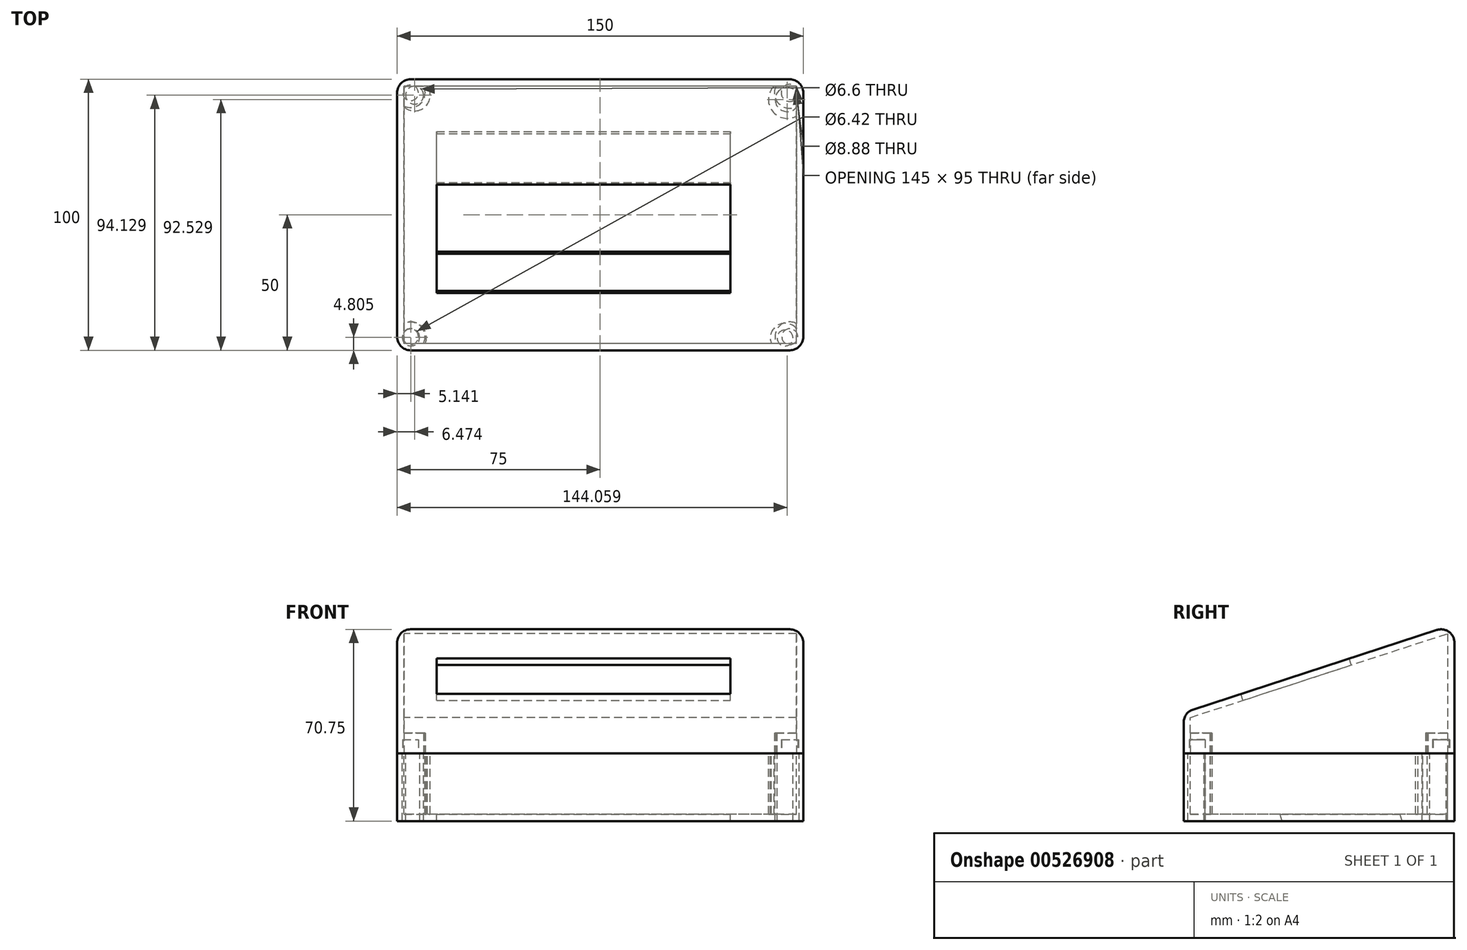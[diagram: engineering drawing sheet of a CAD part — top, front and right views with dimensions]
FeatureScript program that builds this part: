
annotation { "Feature Type Name" : "Feature", "Feature Type Description" : "" }
export const myFeature = defineFeature(function(context is Context, id is Id, definition is map)
    precondition{}
    {
        {
            var Q0;
            Q0=qCreatedBy(makeId("Top.planeOp"),FACE);
            var sketch = newSketch(context, id + "F0", { "sketchPlane" : qUnion([Q0])});
            skLineSegment(sketch, "E0.bottom", {"start": v(75, 50) * mm, "end": v(-75, 50) * mm});
            skLineSegment(sketch, "E0.top", {"start": v(75, -50) * mm, "end": v(-75, -50) * mm});
            skLineSegment(sketch, "E0.left", {"start": v(75, 50) * mm, "end": v(75, -50) * mm});
            skLineSegment(sketch, "E0.right", {"start": v(-75, 50) * mm, "end": v(-75, -50) * mm});
            skPoint(sketch, "E0.middle", {"position": v(0, 0) * mm});
            skSolve(sketch);
        }
        {
            var Q0;
            Q0=makeQuery(id+"F0.imprint","IMPRINT",FACE,{"disambiguationData":[TD([[makeQuery(id+"F0.imprint","IMPRINT",EDGE,{"derivedFrom":sQuery(id+"F0.wireOp",EDGE,"E0.bottom")}),1.0]])]});
            extrude(context, id + "F1", {"entities" : qUnion([Q0]), "depth" : 25 * mm, "offsetDistance" : 25 * mm});
        }
        {
            var Q0;
            Q0=makeQuery(id+"F1.opExtrude","CAP_FACE",FACE,{"disambiguationData":[OSD([sQuery(id+"F0.wireOp",EDGE,"E0.bottom"),sQuery(id+"F0.wireOp",EDGE,"E0.top"),sQuery(id+"F0.wireOp",EDGE,"E0.left"),sQuery(id+"F0.wireOp",EDGE,"E0.right")])],"isStart":false});
            var sketch = newSketch(context, id + "F2", { "sketchPlane" : qUnion([Q0])});
            skCircle(sketch, "E1", {"center": v(-68.53, 44.13) * mm, "radius": 3.3 * mm});
            skCircle(sketch, "E2", {"center": v(-69.86, -45.2) * mm, "radius": 3.21 * mm});
            skCircle(sketch, "E3", {"center": v(68.26, -45.46) * mm, "radius": 2.93 * mm});
            skCircle(sketch, "E4", {"center": v(69.06, 42.53) * mm, "radius": 4.44 * mm});
            skSolve(sketch);
        }
        {
            var Q0;
            Q0 = qSketchRegion(id + "F2", true);
            extrude(context, id + "F3", {"entities" : qUnion([Q0]), "operationType" : NewBodyOperationType.REMOVE, "endBound" : BoundingType.THROUGH_ALL, "oppositeDirection" : true, "depth" : 25 * mm, "offsetDistance" : 25 * mm});
        }
        {
            var Q0;
            Q0=makeQuery(id+"F1.opExtrude","CAP_FACE",FACE,{"disambiguationData":[OSD([sQuery(id+"F0.wireOp",EDGE,"E0.bottom"),sQuery(id+"F0.wireOp",EDGE,"E0.top"),sQuery(id+"F0.wireOp",EDGE,"E0.left"),sQuery(id+"F0.wireOp",EDGE,"E0.right")])],"isStart":false});
            shell(context, id + "F4", {"entities" : qUnion([Q0]), "thickness" : 2.5 * mm});
        }
        {
            var Q0;
            Q0=makeQuery(id+"F1.opExtrude","SWEPT_FACE",FACE,{"disambiguationData":[OSD([sQuery(id+"F0.wireOp",EDGE,"E0.right")])]});
            var sketch = newSketch(context, id + "F5", { "sketchPlane" : qUnion([Q0])});
            skLineSegment(sketch, "E5", {"start": v(-50, 25) * mm, "end": v(50, 25) * mm});
            skLineSegment(sketch, "E6", {"start": v(50, 25) * mm, "end": v(50, 40.03) * mm});
            skLineSegment(sketch, "E7", {"start": v(50, 40.03) * mm, "end": v(-50, 72.64) * mm});
            skLineSegment(sketch, "E8", {"start": v(-50, 72.64) * mm, "end": v(-50, 25) * mm});
            skSolve(sketch);
        }
        {
            var Q0;
            Q0 = qSketchRegion(id + "F5", true);
            var Q1;
            Q1=makeQuery(id+"F1.opExtrude","SWEPT_FACE",FACE,{"disambiguationData":[OSD([sQuery(id+"F0.wireOp",EDGE,"E0.left")])]});
            extrude(context, id + "F6", {"entities" : qUnion([Q0]), "endBound" : BoundingType.UP_TO_SURFACE, "oppositeDirection" : true, "depth" : 25 * mm, "endBoundEntityFace" : qUnion([Q1]), "offsetDistance" : 25 * mm});
        }
        {
            var Q0;
            Q0=makeQuery(id+"F6.opExtrude","SWEPT_FACE",FACE,{"disambiguationData":[OSD([sQuery(id+"F5.wireOp",EDGE,"E5")])]});
            var sketch = newSketch(context, id + "F7", { "sketchPlane" : qUnion([Q0])});
            skCircle(sketch, "E9", {"center": v(-70, 45) * mm, "radius": 2.87 * mm});
            skCircle(sketch, "E10", {"center": v(-70, -45) * mm, "radius": 2.9 * mm});
            skCircle(sketch, "E11", {"center": v(70, -45) * mm, "radius": 3.18 * mm});
            skCircle(sketch, "E12", {"center": v(70, 45) * mm, "radius": 2.94 * mm});
            skSolve(sketch);
        }
        {
            var Q0;
            Q0 = qSketchRegion(id + "F7", true);
            extrude(context, id + "F8", {"entities" : qUnion([Q0]), "operationType" : NewBodyOperationType.REMOVE, "oppositeDirection" : true, "depth" : 5 * mm, "offsetDistance" : 25 * mm});
        }
        {
            var Q0;
            Q0=makeQuery(id+"F6.opExtrude","SWEPT_FACE",FACE,{"disambiguationData":[OSD([sQuery(id+"F5.wireOp",EDGE,"E5")])]});
            shell(context, id + "F9", {"entities" : qUnion([Q0]), "thickness" : 2.5 * mm});
        }
        {
            var Q0;
            Q0=makeQuery(id+"F6.opExtrude","SWEPT_FACE",FACE,{"disambiguationData":[OSD([sQuery(id+"F5.wireOp",EDGE,"E7")])]});
            var sketch = newSketch(context, id + "F10", { "sketchPlane" : qUnion([Q0])});
            skLineSegment(sketch, "E13.bottom", {"start": v(-60.4, -12.93) * mm, "end": v(48.13, -12.93) * mm});
            skLineSegment(sketch, "E13.top", {"start": v(-60.4, 29.2) * mm, "end": v(48.13, 29.2) * mm});
            skLineSegment(sketch, "E13.left", {"start": v(-60.4, -12.93) * mm, "end": v(-60.4, 29.2) * mm});
            skLineSegment(sketch, "E13.right", {"start": v(48.13, -12.93) * mm, "end": v(48.13, 29.2) * mm});
            skSolve(sketch);
        }
        {
            var Q0;
            Q0 = qSketchRegion(id + "F10", true);
            extrude(context, id + "F11", {"entities" : qUnion([Q0]), "operationType" : NewBodyOperationType.REMOVE, "endBound" : BoundingType.THROUGH_ALL, "oppositeDirection" : true, "depth" : 25 * mm, "offsetDistance" : 25 * mm});
        }
        {
            var Q0;
            Q0=makeQuery(id+"F6.opExtrude","SWEPT_EDGE",EDGE,{"disambiguationData":[OSD([sQuery(id+"F5.wireOp",EDGE,"E7"),sQuery(id+"F5.wireOp",EDGE,"E8")])]});
            var Q1;
            Q1=makeQuery(id+"F6.opExtrude","CAP_EDGE",EDGE,{"disambiguationData":[OSD([sQuery(id+"F5.wireOp",EDGE,"E7")])],"isStart":true});
            var Q2;
            Q2=makeQuery(id+"F6.opExtrude","CAP_EDGE",EDGE,{"disambiguationData":[OSD([sQuery(id+"F5.wireOp",EDGE,"E7")])],"isStart":false});
            var Q3;
            Q3=makeQuery(id+"F6.opExtrude","SWEPT_EDGE",EDGE,{"disambiguationData":[OSD([sQuery(id+"F5.wireOp",EDGE,"E6"),sQuery(id+"F5.wireOp",EDGE,"E7")])]});
            var Q4;
            Q4=makeQuery(id+"F6.opExtrude","CAP_EDGE",EDGE,{"disambiguationData":[OSD([sQuery(id+"F5.wireOp",EDGE,"E6")])],"isStart":true});
            var Q5;
            Q5=makeQuery(id+"F6.opExtrude","CAP_EDGE",EDGE,{"disambiguationData":[OSD([sQuery(id+"F5.wireOp",EDGE,"E6")])],"isStart":false});
            var Q6;
            Q6=makeQuery(id+"F6.opExtrude","CAP_EDGE",EDGE,{"disambiguationData":[OSD([sQuery(id+"F5.wireOp",EDGE,"E8")])],"isStart":false});
            var Q7;
            Q7=makeQuery(id+"F6.opExtrude","CAP_EDGE",EDGE,{"disambiguationData":[OSD([sQuery(id+"F5.wireOp",EDGE,"E8")])],"isStart":true});
            fillet(context, id + "F12", {"entities" : qUnion([Q0, Q1, Q2, Q3, Q4, Q5, Q6, Q7]), "radius" : 5 * mm, "tangentPropagation" : true, "allowEdgeOverflow" : false});
        }
        {
            var Q0;
            Q0=makeQuery(id+"F1.opExtrude","SWEPT_EDGE",EDGE,{"disambiguationData":[OSD([sQuery(id+"F0.wireOp",EDGE,"E0.top"),sQuery(id+"F0.wireOp",EDGE,"E0.right")])]});
            var Q1;
            Q1=makeQuery(id+"F1.opExtrude","SWEPT_EDGE",EDGE,{"disambiguationData":[OSD([sQuery(id+"F0.wireOp",EDGE,"E0.top"),sQuery(id+"F0.wireOp",EDGE,"E0.left")])]});
            var Q2;
            Q2=makeQuery(id+"F1.opExtrude","SWEPT_EDGE",EDGE,{"disambiguationData":[OSD([sQuery(id+"F0.wireOp",EDGE,"E0.bottom"),sQuery(id+"F0.wireOp",EDGE,"E0.left")])]});
            var Q3;
            Q3=makeQuery(id+"F1.opExtrude","SWEPT_EDGE",EDGE,{"disambiguationData":[OSD([sQuery(id+"F0.wireOp",EDGE,"E0.bottom"),sQuery(id+"F0.wireOp",EDGE,"E0.right")])]});
            fillet(context, id + "F13", {"entities" : qUnion([Q0, Q1, Q2, Q3]), "radius" : 5 * mm, "tangentPropagation" : true, "allowEdgeOverflow" : false});
        }
    });
